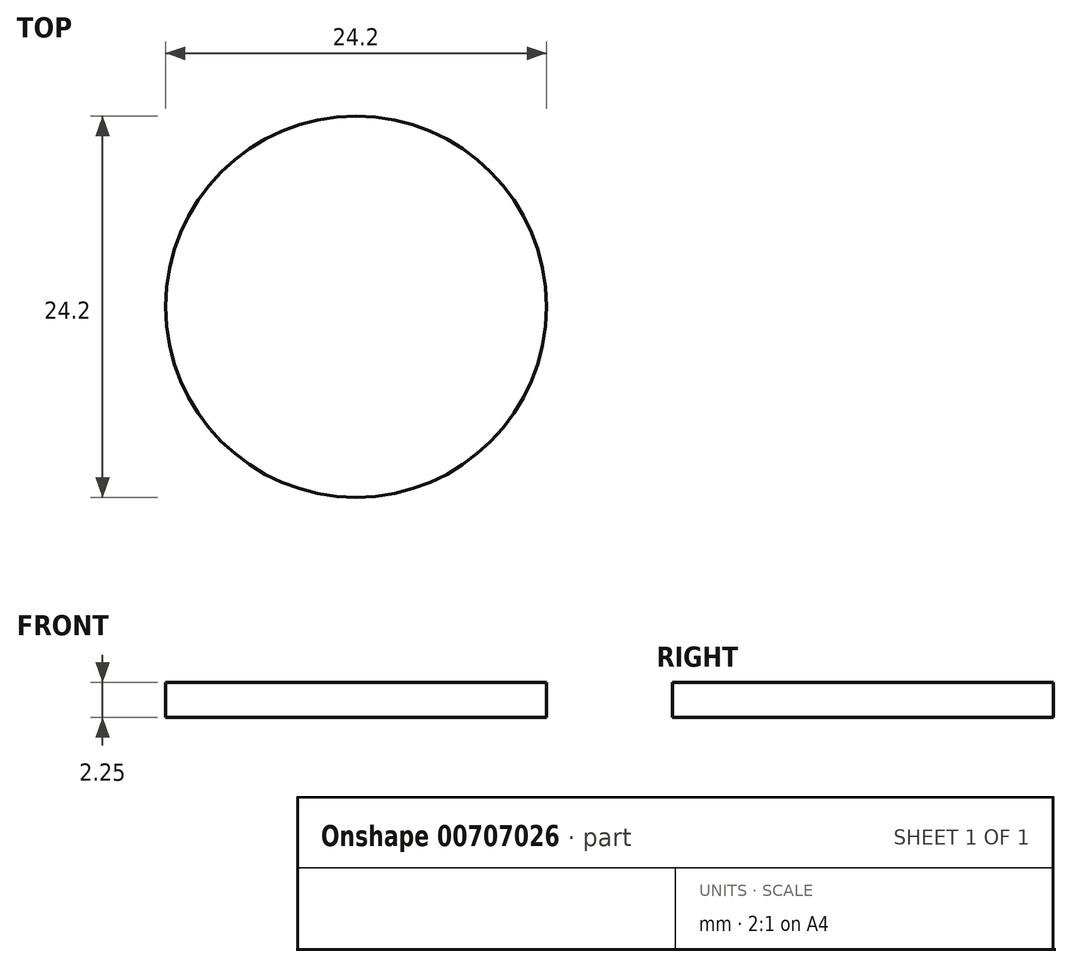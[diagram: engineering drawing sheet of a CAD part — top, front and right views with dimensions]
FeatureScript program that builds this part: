
annotation { "Feature Type Name" : "Feature", "Feature Type Description" : "" }
export const myFeature = defineFeature(function(context is Context, id is Id, definition is map)
    precondition{}
    {
        {
            var Q0;
            Q0=qCreatedBy(makeId("Top.planeOp"),FACE);
            var sketch = newSketch(context, id + "F0", { "sketchPlane" : qUnion([Q0])});
            skCircle(sketch, "E0", {"center": v(0, 0) * mm, "radius": 12.1 * mm});
            skSolve(sketch);
        }
        {
            var Q0;
            Q0 = qSketchRegion(id + "F0", true);
            extrude(context, id + "F1", {"entities" : qUnion([Q0]), "depth" : 2.25 * mm, "offsetDistance" : 25.4 * mm});
        }
    });
